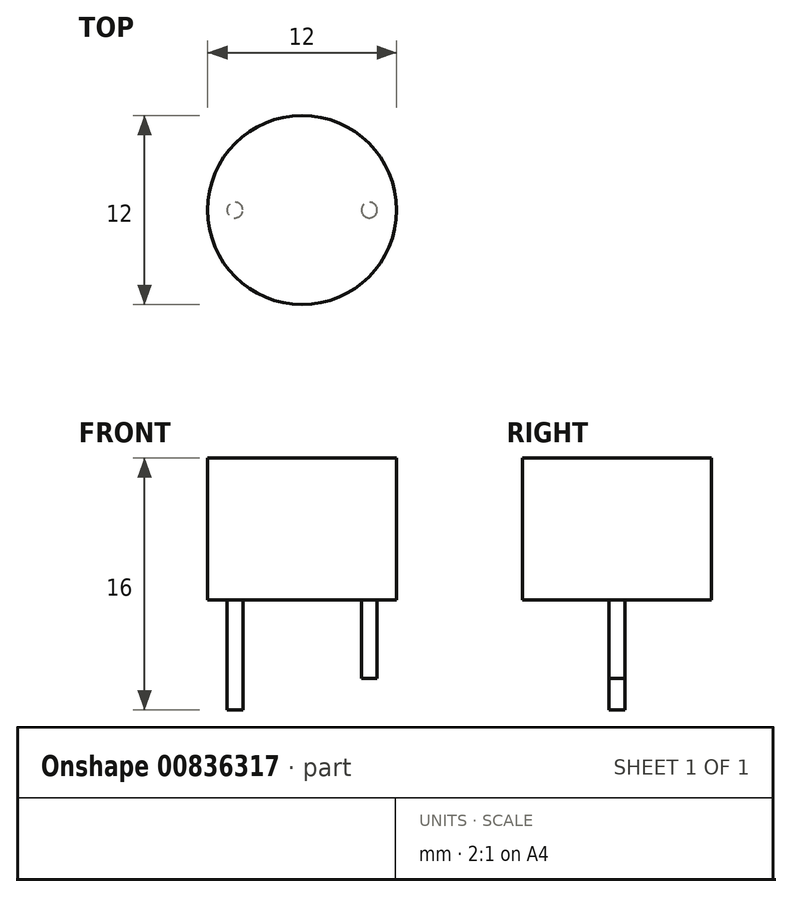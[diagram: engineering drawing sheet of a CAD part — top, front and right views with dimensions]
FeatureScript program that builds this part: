
annotation { "Feature Type Name" : "Feature", "Feature Type Description" : "" }
export const myFeature = defineFeature(function(context is Context, id is Id, definition is map)
    precondition{}
    {
        {
            var Q0;
            Q0=qCreatedBy(makeId("Top.planeOp"),FACE);
            var sketch = newSketch(context, id + "F0", { "sketchPlane" : qUnion([Q0])});
            skCircle(sketch, "E0", {"center": v(0, 0) * mm, "radius": 6 * mm});
            skSolve(sketch);
        }
        {
            var Q0;
            Q0=qSketchRegion(id+"F0",true);
            extrude(context, id + "F1", {"entities" : qUnion([Q0]), "depth" : 9 * mm, "offsetDistance" : 25 * mm});
        }
        {
            var Q0;
            Q0=makeQuery(id+"F1.opExtrude","CAP_FACE",FACE,{"disambiguationData":[OSD([sQuery(id+"F0.wireOp",EDGE,"E0")])],"isStart":true});
            var sketch = newSketch(context, id + "F2", { "sketchPlane" : qUnion([Q0])});
            skCircle(sketch, "E1", {"center": v(4.27, 0) * mm, "radius": 0.5 * mm});
            skCircle(sketch, "E2", {"center": v(-4.27, 0) * mm, "radius": 0.5 * mm});
            skLineSegment(sketch, "E3", {"start": v(0, 0) * mm, "end": v(0, -3.42) * mm, "construction": true});
            skSolve(sketch);
        }
        {
            var Q0;
            Q0=makeQuery(id+"F2.imprint","IMPRINT",FACE,{"disambiguationData":[TD([[makeQuery(id+"F2.imprint","IMPRINT",EDGE,{"derivedFrom":sQuery(id+"F2.wireOp",EDGE,"E2")}),1.0]])]});
            extrude(context, id + "F3", {"entities" : qUnion([Q0]), "operationType" : NewBodyOperationType.ADD, "depth" : 7 * mm, "offsetDistance" : 25 * mm});
        }
        {
            var Q0;
            Q0=makeQuery(id+"F2.imprint","IMPRINT",FACE,{"disambiguationData":[TD([[makeQuery(id+"F2.imprint","IMPRINT",EDGE,{"derivedFrom":sQuery(id+"F2.wireOp",EDGE,"E1")}),1.0]])]});
            extrude(context, id + "F4", {"entities" : qUnion([Q0]), "operationType" : NewBodyOperationType.ADD, "depth" : 5 * mm, "offsetDistance" : 25 * mm});
        }
    });
